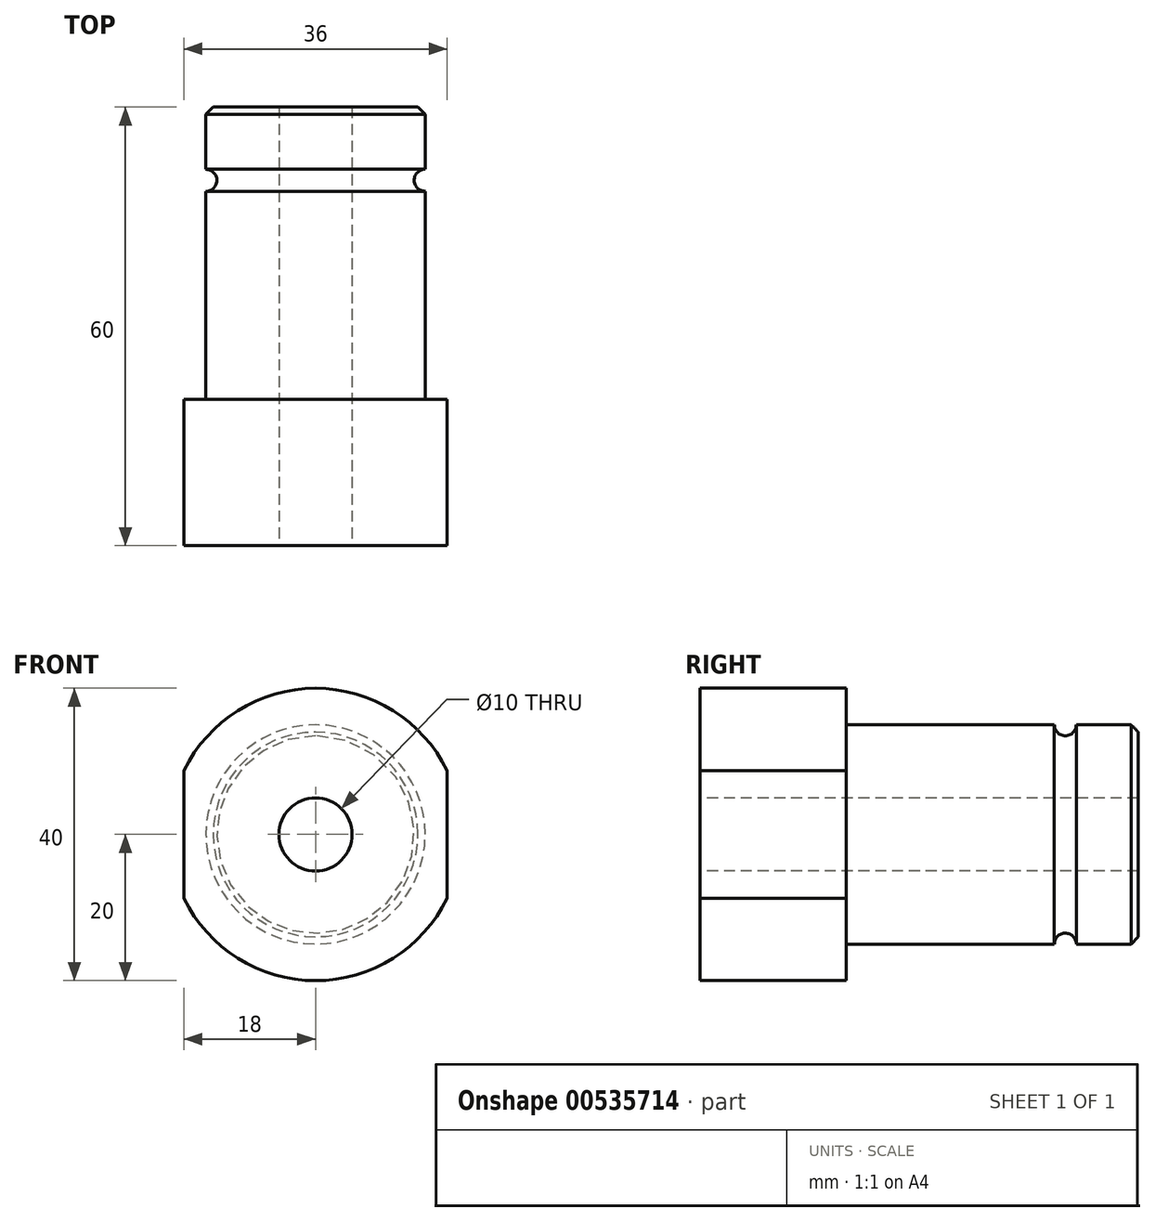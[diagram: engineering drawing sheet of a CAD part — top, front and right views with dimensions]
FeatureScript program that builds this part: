
annotation { "Feature Type Name" : "Feature", "Feature Type Description" : "" }
export const myFeature = defineFeature(function(context is Context, id is Id, definition is map)
    precondition{}
    {
        {
            var Q0;
            Q0=qCreatedBy(makeId("Front.planeOp"),FACE);
            var sketch = newSketch(context, id + "F0", { "sketchPlane" : qUnion([Q0])});
            skCircle(sketch, "E0", {"center": v(0, 0) * mm, "radius": 20 * mm});
            skLineSegment(sketch, "E1", {"start": v(0, 0) * mm, "end": v(-18, 0) * mm});
            skLineSegment(sketch, "E2", {"start": v(-18, 0) * mm, "end": v(-18, 23.72) * mm});
            skLineSegment(sketch, "E3", {"start": v(0, 0) * mm, "end": v(18, 0) * mm});
            skLineSegment(sketch, "E4", {"start": v(18, 0) * mm, "end": v(18, 41.46) * mm});
            skLineSegment(sketch, "E5", {"start": v(-18, 0) * mm, "end": v(-18, -28.6) * mm});
            skLineSegment(sketch, "E6", {"start": v(18, 0) * mm, "end": v(18, -29.69) * mm});
            skSolve(sketch);
        }
        {
            var Q0;
            {var subQ0=sQuery(id+"F0.wireOp",EDGE,"E2");var subQ3=sQuery(id+"F0.wireOp",EDGE,"E0");var subQ4=makeQuery(id+"F0.imprint","INTERSECT",VERTEX,{"derivedFrom":[subQ3,subQ0]});Q0=makeQuery(id+"F0.imprint","IMPRINT",FACE,{"disambiguationData":[TD([[makeQuery(id+"F0.imprint","IMPRINT",EDGE,{"disambiguationData":[TD([[subQ4,1.0]])],"derivedFrom":subQ3}),1.0]])]});}
            var Q1;
            {var subQ7=sQuery(id+"F0.wireOp",EDGE,"E5");var subQ9=sQuery(id+"F0.wireOp",EDGE,"E0");var subQ10=makeQuery(id+"F0.imprint","INTERSECT",VERTEX,{"derivedFrom":[subQ9,subQ7]});Q1=makeQuery(id+"F0.imprint","IMPRINT",FACE,{"disambiguationData":[TD([[makeQuery(id+"F0.imprint","IMPRINT",EDGE,{"disambiguationData":[TD([[subQ10,-1.0]])],"derivedFrom":subQ9}),1.0]])]});}
            extrude(context, id + "F1", {"entities" : qUnion([Q0, Q1]), "depth" : 20 * mm, "offsetDistance" : 25 * mm});
        }
        {
            var Q0;
            Q0=qCreatedBy(makeId("Right.planeOp"),FACE);
            var sketch = newSketch(context, id + "F2", { "sketchPlane" : qUnion([Q0])});
            skLineSegment(sketch, "E7", {"start": v(0, 0) * mm, "end": v(0, 15) * mm});
            skLineSegment(sketch, "E8", {"start": v(0, 15) * mm, "end": v(40, 15) * mm});
            skLineSegment(sketch, "E9", {"start": v(40, 15) * mm, "end": v(40, 0) * mm});
            skLineSegment(sketch, "E10", {"start": v(40, 0) * mm, "end": v(0, 0) * mm});
            skLineSegment(sketch, "E11", {"start": v(40, 15) * mm, "end": v(30, 15) * mm});
            skCircle(sketch, "E12", {"center": v(30, 15) * mm, "radius": 1.5 * mm});
            skLineSegment(sketch, "E13", {"start": v(40, 15) * mm, "end": v(39, 15) * mm});
            skLineSegment(sketch, "E14", {"start": v(39, 15) * mm, "end": v(40, 14) * mm});
            skLineSegment(sketch, "E15", {"start": v(40, 15) * mm, "end": v(40, 14) * mm});
            skSolve(sketch);
        }
        {
            var Q0;
            Q0=makeQuery(id+"F2.imprint","IMPRINT",FACE,{"disambiguationData":[TD([[makeQuery(id+"F2.imprint","IMPRINT",EDGE,{"derivedFrom":sQuery(id+"F2.wireOp",EDGE,"E7")}),-1.0]])]});
            var Q1;
            Q1=sQuery(id+"F2.wireOp",EDGE,"E10");
            revolve(context, id + "F3", {"operationType" : NewBodyOperationType.ADD, "entities" : qUnion([Q0]), "axis" : qUnion([Q1]), "revolveType" : RevolveType.FULL});
        }
        {
            var Q0;
            Q0=makeQuery(id+"F1.opExtrude","CAP_FACE",FACE,{"disambiguationData":[OSD([sQuery(id+"F0.wireOp",EDGE,"E0"),sQuery(id+"F0.wireOp",EDGE,"E2"),sQuery(id+"F0.wireOp",EDGE,"E4"),sQuery(id+"F0.wireOp",EDGE,"E5"),sQuery(id+"F0.wireOp",EDGE,"E6")])],"isStart":false});
            var sketch = newSketch(context, id + "F4", { "sketchPlane" : qUnion([Q0])});
            skCircle(sketch, "E16", {"center": v(0, 0) * mm, "radius": 5 * mm});
            skSolve(sketch);
        }
        {
            var Q0;
            Q0=makeQuery(id+"F4.imprint","IMPRINT",FACE,{"disambiguationData":[TD([[makeQuery(id+"F4.imprint","IMPRINT",EDGE,{"derivedFrom":sQuery(id+"F4.wireOp",EDGE,"E16")}),1.0]])]});
            extrude(context, id + "F5", {"entities" : qUnion([Q0]), "operationType" : NewBodyOperationType.REMOVE, "endBound" : BoundingType.THROUGH_ALL, "oppositeDirection" : true, "depth" : 25 * mm, "offsetDistance" : 25 * mm});
        }
    });
